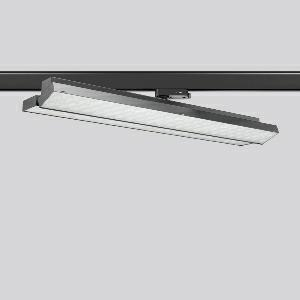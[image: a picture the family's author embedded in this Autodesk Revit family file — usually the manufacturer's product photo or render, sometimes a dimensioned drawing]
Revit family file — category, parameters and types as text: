
# Revit family: tx-move_742162_003_1b9d
name_source: partatom
category: Lighting Fixtures
units: mm (PartAtom-declared; Revit-internal decimal feet)

## family parameters
Cut with Voids When Loaded = No
Host = Face
Light Source = No
Part Type = Normal
Room Calculation Point = No
Round Connector Dimension = Use Diameter
Shared = No

## types (1)
- MultiLumen 1 (1 x LED Modul 830, 2925 lm, 3000)
    Apparent Load = 41 VA
    CIE Flux Codes = 77 96 99 100 100
    Color Rendering = 80
    Color Temperature = 3000
    Default Elevation = 1800 mm
    Description = Series: TX-MOVE
Multifunctional surface-mounted spotlight for area lighting. Very flat design. Housing: sheet steel, powder-coated. Rotation range: 356°. Swivel range: 90°. Consistent alignment possible with visible tilt scale. High-efficiency LED units with optimum light control thanks to clear plastic (PC) lens optics. Spezielle Mikrostrukturen reduzieren Gelbsaum. Symmetrical light distribution. With multi adaptor for 3-circuit tracks 230 V. Suitable for Track on ceiling. MultiLumen: Luminous flux adjustable in 3 steps. Factory setting is the highest luminous flux. Environmentally friendly and resource-saving due to replaceable and recyclable components. 
Colour: deep black, matt (RAL 9005)
Length: 570 mm
Width: 119 mm
Height: 92 mm
Lamp: LED
Socket: without socket
Colour temperature: 3000K
Colour rendering index (CRI): 80
System power: 41 W
Rated luminous flux: 5850 lm
Luminous efficiency: 143 lm/W
System power 2: 57 W
Rated luminous flux 2: 7950 lm
Luminous efficiency 2: 139 lm/W
System power 3: 73 W
Rated luminous flux 3: 9700 lm
Luminous efficiency 3: 133 lm/W
Control gear: Regulated power supply
Protection class: I
Type of protection: IP 20
    Height = 75 mm
    Lamp = 1 x LED Modul 830
    Lamp Light Flux = 2925 lm
    Lamp count = 1
    Length = 569 mm
    Lifetime = 50000 h
    Luminous efficacy = 143 lm/W
    Manufacturer = RZB
    ModVariant = No
    Model = 742162.003
    Mounting Place = Ceiling
    Mounting Type = Surface mounted
    Number of Poles = 1
    OnlyDefault = Yes
    Power Factor = 1
    Product Name = TX-MOVE
    Product group = Track mounted projectors
    ProductGroupID = 301
    Protection Class = Protection class I
    Protection Degree = IP 20
    RLX_Detail_Level = 1
    RLX_Emergency_Light_Flux = 0 lm
    RLX_Emergency_Type = 0
    RLX_Emergency_Type_DB = No
    RlxData = <blob elided: 36945 chars, md5=9d0378f1>
    Socket = socket
    Standby Power = 0 W
    System Light Flux = 5850 lm
    System Power = 41 W
    Type Comments = MultiLumen 1
    Type Image = 742162.003.jpg
    URL = http://relux.com
    VarID = multilumen_1
    Voltage = 0 V
    Weight = 0.00 kg
    Width = 119 mm

## geometry (parser evidence)
native form markers: Blend x4, Sweep x15
no freeform markers — native parametric forms only
